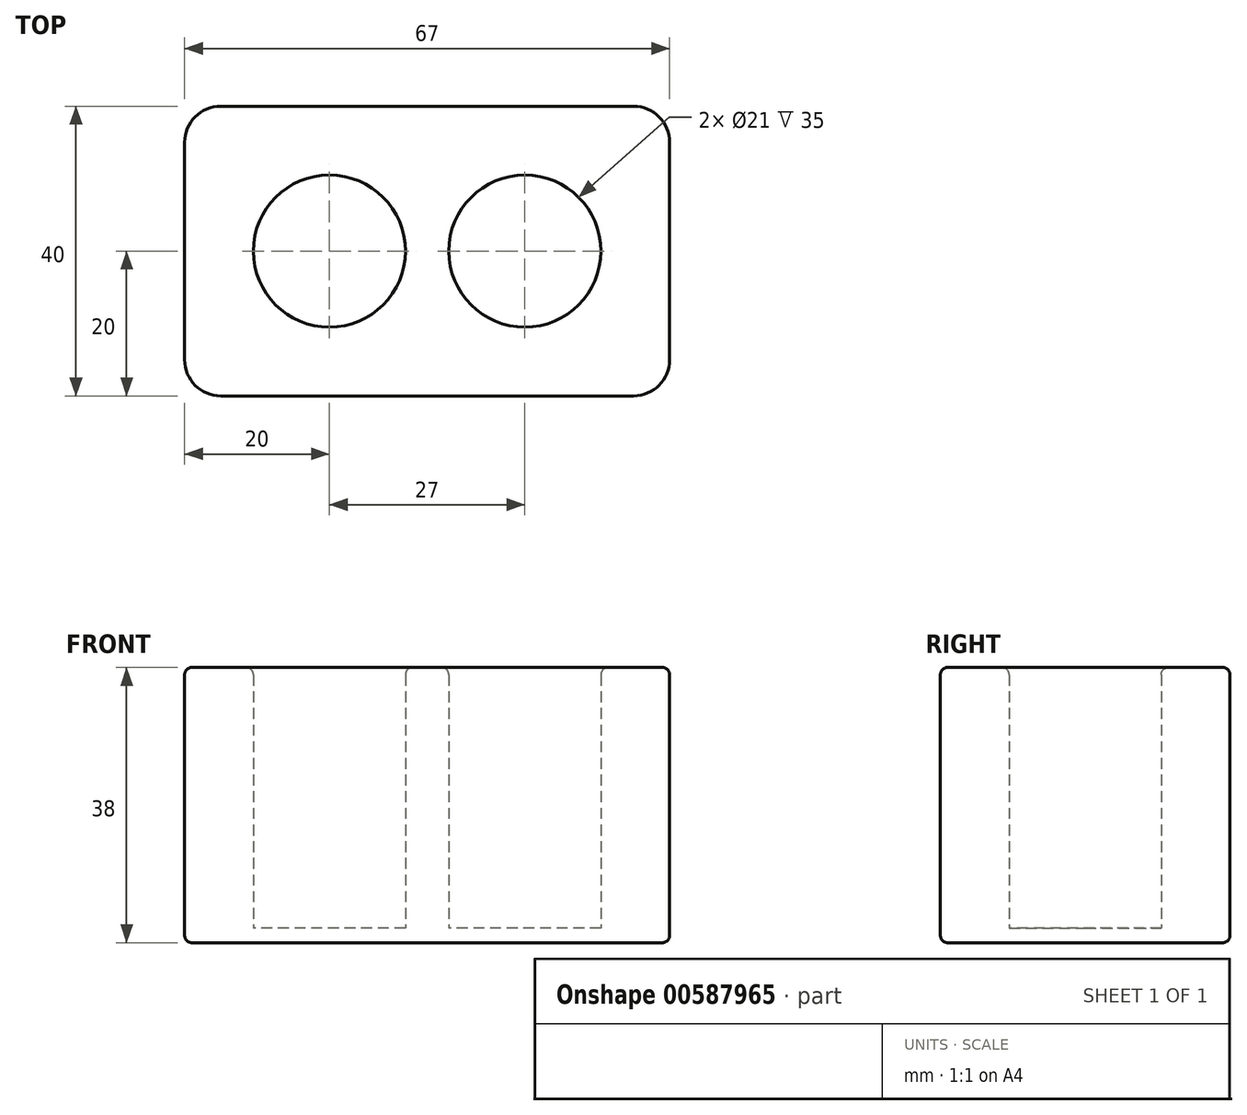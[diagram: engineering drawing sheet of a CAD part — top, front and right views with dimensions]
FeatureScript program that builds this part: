
annotation { "Feature Type Name" : "Feature", "Feature Type Description" : "" }
export const myFeature = defineFeature(function(context is Context, id is Id, definition is map)
    precondition{}
    {
        {
            var Q0;
            Q0=qCreatedBy(makeId("Top.planeOp"),FACE);
            var sketch = newSketch(context, id + "F0", { "sketchPlane" : qUnion([Q0])});
            skLineSegment(sketch, "E0.bottom", {"start": v(-33.5, 20) * mm, "end": v(33.5, 20) * mm});
            skLineSegment(sketch, "E0.top", {"start": v(-33.5, -20) * mm, "end": v(33.5, -20) * mm});
            skLineSegment(sketch, "E0.left", {"start": v(-33.5, 20) * mm, "end": v(-33.5, -20) * mm});
            skLineSegment(sketch, "E0.right", {"start": v(33.5, 20) * mm, "end": v(33.5, -20) * mm});
            skPoint(sketch, "E0.middle", {"position": v(0, 0) * mm});
            skCircle(sketch, "E1", {"center": v(-13.5, 0) * mm, "radius": 10.5 * mm});
            skCircle(sketch, "E2", {"center": v(13.5, 0) * mm, "radius": 10.5 * mm});
            skSolve(sketch);
        }
        {
            var Q0;
            Q0 = qSketchRegion(id + "F0", true);
            var Q1;
            Q1=makeQuery(id+"F0.imprint","IMPRINT",FACE,{"disambiguationData":[TD([[makeQuery(id+"F0.imprint","IMPRINT",EDGE,{"derivedFrom":sQuery(id+"F0.wireOp",EDGE,"E0.bottom")}),-1.0]])]});
            extrude(context, id + "F1", {"entities" : qUnion([Q0, Q1]), "depth" : 36 * mm, "offsetDistance" : 25 * mm});
        }
        {
            var Q0;
            Q0=makeQuery(id+"F1.opExtrude","CAP_FACE",FACE,{"disambiguationData":[OSD([sQuery(id+"F0.wireOp",EDGE,"E0.bottom"),sQuery(id+"F0.wireOp",EDGE,"E0.top"),sQuery(id+"F0.wireOp",EDGE,"E0.left"),sQuery(id+"F0.wireOp",EDGE,"E0.right"),sQuery(id+"F0.wireOp",EDGE,"E1"),sQuery(id+"F0.wireOp",EDGE,"E2")])],"isStart":true});
            var sketch = newSketch(context, id + "F2", { "sketchPlane" : qUnion([Q0])});
            skLineSegment(sketch, "E3.bottom", {"start": v(33.5, -20) * mm, "end": v(-33.5, -20) * mm});
            skLineSegment(sketch, "E3.top", {"start": v(33.5, 20) * mm, "end": v(-33.5, 20) * mm});
            skLineSegment(sketch, "E3.left", {"start": v(33.5, -20) * mm, "end": v(33.5, 20) * mm});
            skLineSegment(sketch, "E3.right", {"start": v(-33.5, -20) * mm, "end": v(-33.5, 20) * mm});
            skSolve(sketch);
        }
        {
            var Q0;
            Q0 = qSketchRegion(id + "F2", true);
            extrude(context, id + "F3", {"entities" : qUnion([Q0]), "operationType" : NewBodyOperationType.ADD, "depth" : 2 * mm, "offsetDistance" : 25 * mm});
        }
        {
            var Q0;
            Q0=makeQuery(id+"F1.opExtrude","CAP_FACE",FACE,{"disambiguationData":[OSD([sQuery(id+"F0.wireOp",EDGE,"E0.bottom"),sQuery(id+"F0.wireOp",EDGE,"E0.top"),sQuery(id+"F0.wireOp",EDGE,"E0.left"),sQuery(id+"F0.wireOp",EDGE,"E0.right"),sQuery(id+"F0.wireOp",EDGE,"E1"),sQuery(id+"F0.wireOp",EDGE,"E2")])],"isStart":false});
            var Q1;
            Q1=makeQuery(id+"F3.opExtrude","CAP_FACE",FACE,{"disambiguationData":[OSD([sQuery(id+"F2.wireOp",EDGE,"E3.bottom"),sQuery(id+"F2.wireOp",EDGE,"E3.top"),sQuery(id+"F2.wireOp",EDGE,"E3.left"),sQuery(id+"F2.wireOp",EDGE,"E3.right")])],"isStart":false});
            fillet(context, id + "F4", {"entities" : qUnion([Q0, Q1]), "radius" : 1 * mm, "tangentPropagation" : true, "allowEdgeOverflow" : false});
        }
        {
            var Q0;
            Q0=makeQuery(id+"F3.boolean.opBoolean","MERGE",EDGE,{"derivedFrom":[makeQuery(id+"F1.opExtrude","SWEPT_EDGE",EDGE,{"disambiguationData":[OSD([sQuery(id+"F0.wireOp",EDGE,"E0.bottom"),sQuery(id+"F0.wireOp",EDGE,"E0.right")])]}),makeQuery(id+"F3.opExtrude","SWEPT_EDGE",EDGE,{"disambiguationData":[OSD([sQuery(id+"F2.wireOp",EDGE,"E3.bottom"),sQuery(id+"F2.wireOp",EDGE,"E3.left")])]})]});
            var Q1;
            Q1=makeQuery(id+"F3.boolean.opBoolean","MERGE",EDGE,{"derivedFrom":[makeQuery(id+"F1.opExtrude","SWEPT_EDGE",EDGE,{"disambiguationData":[OSD([sQuery(id+"F0.wireOp",EDGE,"E0.top"),sQuery(id+"F0.wireOp",EDGE,"E0.right")])]}),makeQuery(id+"F3.opExtrude","SWEPT_EDGE",EDGE,{"disambiguationData":[OSD([sQuery(id+"F2.wireOp",EDGE,"E3.top"),sQuery(id+"F2.wireOp",EDGE,"E3.left")])]})]});
            var Q2;
            Q2=makeQuery(id+"F3.boolean.opBoolean","MERGE",EDGE,{"derivedFrom":[makeQuery(id+"F1.opExtrude","SWEPT_EDGE",EDGE,{"disambiguationData":[OSD([sQuery(id+"F0.wireOp",EDGE,"E0.top"),sQuery(id+"F0.wireOp",EDGE,"E0.left")])]}),makeQuery(id+"F3.opExtrude","SWEPT_EDGE",EDGE,{"disambiguationData":[OSD([sQuery(id+"F2.wireOp",EDGE,"E3.top"),sQuery(id+"F2.wireOp",EDGE,"E3.right")])]})]});
            var Q3;
            Q3=makeQuery(id+"F3.boolean.opBoolean","MERGE",EDGE,{"derivedFrom":[makeQuery(id+"F1.opExtrude","SWEPT_EDGE",EDGE,{"disambiguationData":[OSD([sQuery(id+"F0.wireOp",EDGE,"E0.bottom"),sQuery(id+"F0.wireOp",EDGE,"E0.left")])]}),makeQuery(id+"F3.opExtrude","SWEPT_EDGE",EDGE,{"disambiguationData":[OSD([sQuery(id+"F2.wireOp",EDGE,"E3.bottom"),sQuery(id+"F2.wireOp",EDGE,"E3.right")])]})]});
            fillet(context, id + "F5", {"entities" : qUnion([Q0, Q1, Q2, Q3]), "radius" : 5 * mm, "tangentPropagation" : true, "allowEdgeOverflow" : false});
        }
    });
